# Revit family: Furniture-Counter_Top-KOHLER-Solid_Expressions-K-5436_1
name_source: partatom
category: Specialty Equipment
units: mm (PartAtom-declared; Revit-internal decimal feet)

## family parameters
Cut with Voids When Loaded = No
Host = Face
OmniClass Number = 23.31.25.00
OmniClass Title = Toilet and Bath Specialties
Part Type = Normal
Room Calculation Point = No
Round Connector Dimension = Use Diameter
Shared = No

## types (1)
- S33-White Expressions
    ADA Compliant = No
    Assembly Code = C1030200
    Date Modified = 08/28/2023
    Default Elevation = 36"
    Description = 25 inch vanity top without cutout
    Finish = Kohler-Solid_Surface-S33-White_Expressions
    Height = 1"
    Length = 22 3/8"
    Manufacturer = Kohler Co.
    Master Format 2014 = 10 28 00
    Master Format 2014 Name = Toilet, Bath, and Laundry Accessories
    Material = Solid Surface
    Model = K-5436-S33
    Product Documentation Link = https://www.us.kohler.com
    Product Name = Solid Expressions
    Product Page URL = http://www.us.kohler.com
    Type = 1
    URL = https://www.us.kohler.com
    WaterSense Certified = No
    Width = 25"

## geometry (parser evidence)
native form markers: Sweep x9
no freeform markers — native parametric forms only
